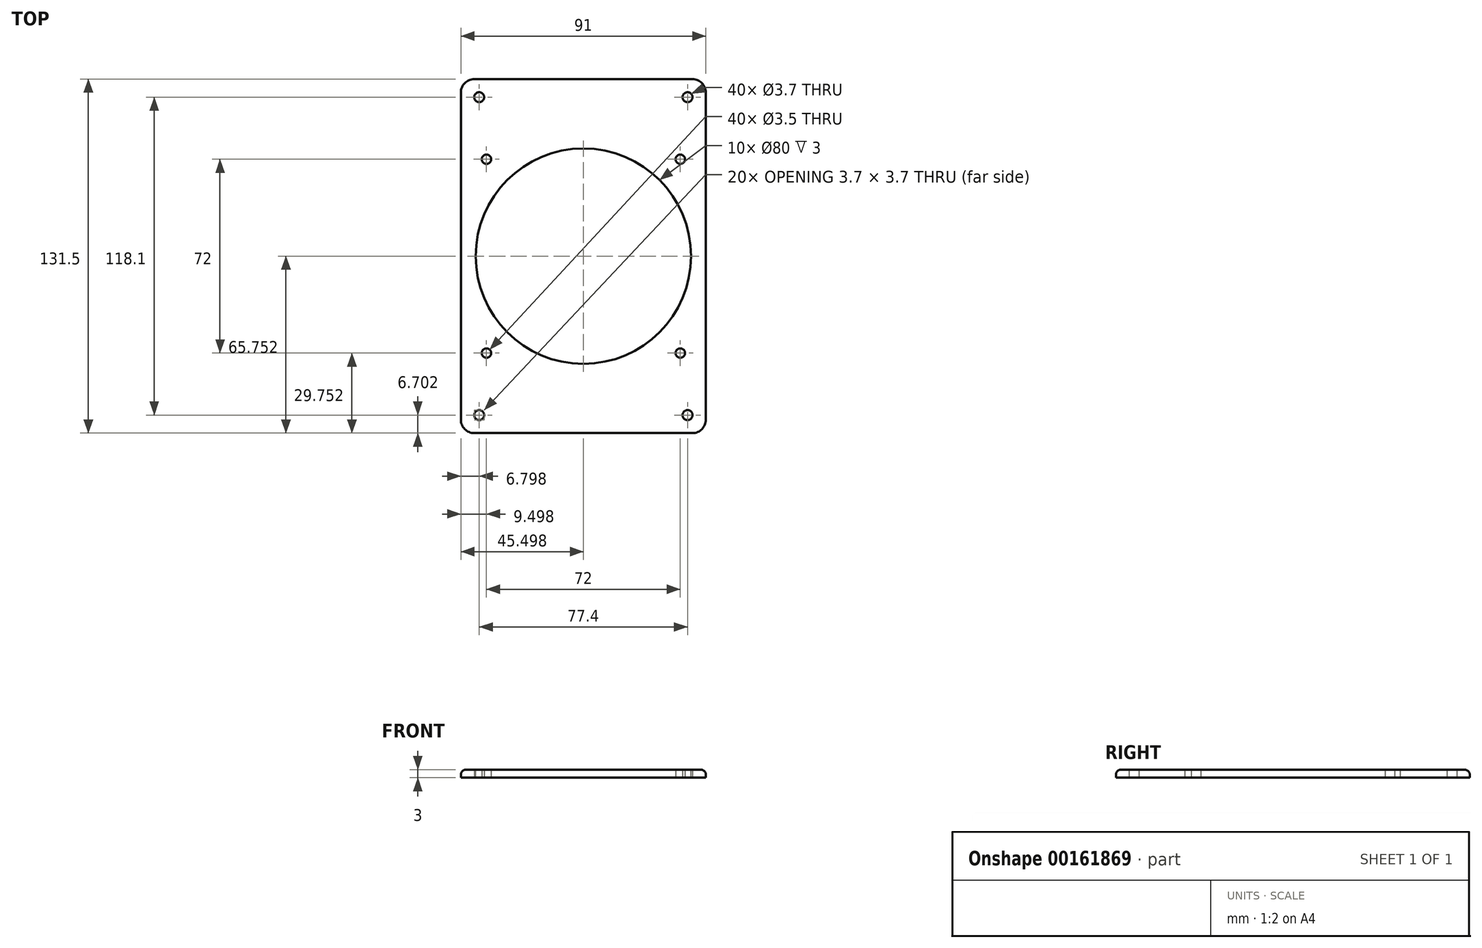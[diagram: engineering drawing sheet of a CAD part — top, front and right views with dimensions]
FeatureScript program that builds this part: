
annotation { "Feature Type Name" : "Feature", "Feature Type Description" : "" }
export const myFeature = defineFeature(function(context is Context, id is Id, definition is map)
    precondition{}
    {
        {
            var Q0;
            Q0=qCreatedBy(makeId("Top.planeOp"),FACE);
            var sketch = newSketch(context, id + "F0", { "sketchPlane" : qUnion([Q0])});
            skLineSegment(sketch, "E0.bottom", {"start": v(54.26, -33.58) * mm, "end": v(-26.74, -33.58) * mm});
            skLineSegment(sketch, "E0.top", {"start": v(54.26, 97.92) * mm, "end": v(-26.74, 97.92) * mm});
            skLineSegment(sketch, "E0.left", {"start": v(59.26, -28.58) * mm, "end": v(59.26, 92.92) * mm});
            skLineSegment(sketch, "E0.right", {"start": v(-31.74, -28.58) * mm, "end": v(-31.74, 92.92) * mm});
            skLineSegment(sketch, "E1.bottom", {"start": v(80.42, 31.08) * mm, "end": v(80.93, 31.08) * mm});
            skLineSegment(sketch, "E1.top", {"start": v(80.42, 14.88) * mm, "end": v(80.93, 14.88) * mm});
            skPoint(sketch, "E2.visualSharp", {"position": v(-31.74, 97.92) * mm});
            skArc(sketch, "E2.filletArc", {"start": v(-26.74, 97.92) * mm, "mid": v(-30.28, 96.46) * mm, "end": v(-31.74, 92.92) * mm});
            skPoint(sketch, "E3.visualSharp", {"position": v(-31.74, -33.58) * mm});
            skArc(sketch, "E3.filletArc", {"start": v(-31.74, -28.58) * mm, "mid": v(-30.28, -32.11) * mm, "end": v(-26.74, -33.58) * mm});
            skPoint(sketch, "E4.visualSharp", {"position": v(59.26, 97.92) * mm});
            skArc(sketch, "E4.filletArc", {"start": v(59.26, 92.92) * mm, "mid": v(57.8, 96.46) * mm, "end": v(54.26, 97.92) * mm});
            skPoint(sketch, "E5.visualSharp", {"position": v(59.26, -33.58) * mm});
            skArc(sketch, "E5.filletArc", {"start": v(54.26, -33.58) * mm, "mid": v(57.8, -32.11) * mm, "end": v(59.26, -28.58) * mm});
            skSolve(sketch);
        }
        {
            var Q0;
            Q0=makeQuery(id+"F0.imprint","IMPRINT",FACE,{"disambiguationData":[TD([[makeQuery(id+"F0.imprint","IMPRINT",EDGE,{"derivedFrom":sQuery(id+"F0.wireOp",EDGE,"E0.bottom")}),-1.0]])]});
            extrude(context, id + "F1", {"entities" : qUnion([Q0]), "depth" : 3 * mm});
        }
        {
            var Q0;
            Q0=makeQuery(id+"F1.opExtrude","CAP_FACE",FACE,{"disambiguationData":[OSD([sQuery(id+"F0.wireOp",EDGE,"E0.bottom"),sQuery(id+"F0.wireOp",EDGE,"E0.top"),sQuery(id+"F0.wireOp",EDGE,"E0.left"),sQuery(id+"F0.wireOp",EDGE,"E0.right"),sQuery(id+"F0.wireOp",EDGE,"E2.filletArc"),sQuery(id+"F0.wireOp",EDGE,"E3.filletArc"),sQuery(id+"F0.wireOp",EDGE,"E4.filletArc"),sQuery(id+"F0.wireOp",EDGE,"E5.filletArc")])],"isStart":false});
            var sketch = newSketch(context, id + "F2", { "sketchPlane" : qUnion([Q0])});
            skLineSegment(sketch, "E6.bottom", {"start": v(-24.94, 91.22) * mm, "end": v(52.46, 91.22) * mm});
            skLineSegment(sketch, "E6.top", {"start": v(-24.94, -26.88) * mm, "end": v(52.46, -26.88) * mm});
            skLineSegment(sketch, "E6.left", {"start": v(-24.94, 91.22) * mm, "end": v(-24.94, -26.88) * mm});
            skLineSegment(sketch, "E6.right", {"start": v(52.46, 91.22) * mm, "end": v(52.46, -26.88) * mm});
            skPoint(sketch, "E7", {"position": v(-24.94, 91.22) * mm});
            skPoint(sketch, "E8", {"position": v(52.46, 91.22) * mm});
            skPoint(sketch, "E9", {"position": v(52.46, -26.88) * mm});
            skPoint(sketch, "E10", {"position": v(-24.94, -26.88) * mm});
            skSolve(sketch);
        }
        {
            var Q0;
            Q0=sQuery(id+"F2.wireOp",VERTEX,"E7");
            var Q1;
            Q1=sQuery(id+"F2.wireOp",VERTEX,"E8");
            var Q2;
            Q2=sQuery(id+"F2.wireOp",VERTEX,"E9");
            var Q3;
            Q3=sQuery(id+"F2.wireOp",VERTEX,"E10");
            var Q4;
            Q4=makeQuery(id+"F1.opExtrude","SWEPT_BODY",BODY,{"disambiguationData":[OSD([sQuery(id+"F0.wireOp",EDGE,"E0.bottom"),sQuery(id+"F0.wireOp",EDGE,"E0.top"),sQuery(id+"F0.wireOp",EDGE,"E0.left"),sQuery(id+"F0.wireOp",EDGE,"E0.right"),sQuery(id+"F0.wireOp",EDGE,"E2.filletArc"),sQuery(id+"F0.wireOp",EDGE,"E3.filletArc"),sQuery(id+"F0.wireOp",EDGE,"E4.filletArc"),sQuery(id+"F0.wireOp",EDGE,"E5.filletArc")])]});
            hole(context, id + "F3", {"style" : HoleStyle.SIMPLE, "endStyle" : HoleEndStyle.THROUGH, "holeDiameter" : 3.7 * mm, "locations" : qUnion([Q0, Q1, Q2, Q3]), "scope" : qUnion([Q4]), "isTappedThrough" : true});
        }
        {
            var Q0;
            Q0=makeQuery(id+"F1.opExtrude","CAP_FACE",FACE,{"disambiguationData":[OSD([sQuery(id+"F0.wireOp",EDGE,"E0.bottom"),sQuery(id+"F0.wireOp",EDGE,"E0.top"),sQuery(id+"F0.wireOp",EDGE,"E0.left"),sQuery(id+"F0.wireOp",EDGE,"E0.right"),sQuery(id+"F0.wireOp",EDGE,"E2.filletArc"),sQuery(id+"F0.wireOp",EDGE,"E3.filletArc"),sQuery(id+"F0.wireOp",EDGE,"E4.filletArc"),sQuery(id+"F0.wireOp",EDGE,"E5.filletArc")])],"isStart":false});
            var sketch = newSketch(context, id + "F4", { "sketchPlane" : qUnion([Q0])});
            skCircle(sketch, "E11", {"center": v(13.76, 32.17) * mm, "radius": 40 * mm});
            skLineSegment(sketch, "E12.bottom", {"start": v(-22.24, 68.17) * mm, "end": v(49.76, 68.17) * mm});
            skLineSegment(sketch, "E12.top", {"start": v(-22.24, -3.83) * mm, "end": v(49.76, -3.83) * mm});
            skLineSegment(sketch, "E12.left", {"start": v(-22.24, 68.17) * mm, "end": v(-22.24, -3.83) * mm});
            skLineSegment(sketch, "E12.right", {"start": v(49.76, 68.17) * mm, "end": v(49.76, -3.83) * mm});
            skPoint(sketch, "E13", {"position": v(-22.24, 68.17) * mm});
            skPoint(sketch, "E14", {"position": v(49.76, 68.17) * mm});
            skPoint(sketch, "E15", {"position": v(49.76, -3.83) * mm});
            skPoint(sketch, "E16", {"position": v(-22.24, -3.83) * mm});
            skSolve(sketch);
        }
        {
            var Q0;
            Q0=makeQuery(id+"F1.opExtrude","CAP_FACE",FACE,{"disambiguationData":[OSD([sQuery(id+"F0.wireOp",EDGE,"E0.bottom"),sQuery(id+"F0.wireOp",EDGE,"E0.top"),sQuery(id+"F0.wireOp",EDGE,"E0.left"),sQuery(id+"F0.wireOp",EDGE,"E0.right"),sQuery(id+"F0.wireOp",EDGE,"E2.filletArc"),sQuery(id+"F0.wireOp",EDGE,"E3.filletArc"),sQuery(id+"F0.wireOp",EDGE,"E4.filletArc"),sQuery(id+"F0.wireOp",EDGE,"E5.filletArc")])],"isStart":false});
            var sketch = newSketch(context, id + "F5", { "sketchPlane" : qUnion([Q0])});
            skCircle(sketch, "E17", {"center": v(13.76, 32.17) * mm, "radius": 40 * mm});
            skPoint(sketch, "E18", {"position": v(-21.85, 68.29) * mm});
            skPoint(sketch, "E19", {"position": v(49.62, 68.29) * mm});
            skPoint(sketch, "E20", {"position": v(50.13, -3.7) * mm});
            skPoint(sketch, "E21", {"position": v(-22.02, -4.03) * mm});
            skSolve(sketch);
        }
        {
            var Q0;
            Q0=makeQuery(id+"F5.imprint","IMPRINT",FACE,{"disambiguationData":[TD([[makeQuery(id+"F5.imprint","IMPRINT",EDGE,{"derivedFrom":sQuery(id+"F5.wireOp",EDGE,"E17")}),1.0]])]});
            extrude(context, id + "F6", {"entities" : qUnion([Q0]), "operationType" : NewBodyOperationType.REMOVE, "oppositeDirection" : true, "depth" : 25 * mm});
        }
        {
            var Q0;
            Q0=makeQuery(id+"F1.opExtrude","CAP_EDGE",EDGE,{"disambiguationData":[OSD([sQuery(id+"F0.wireOp",EDGE,"E0.right")])],"isStart":false});
            var Q1;
            Q1=makeQuery(id+"F1.opExtrude","CAP_EDGE",EDGE,{"disambiguationData":[OSD([sQuery(id+"F0.wireOp",EDGE,"E0.top")])],"isStart":false});
            fillet(context, id + "F7", {"entities" : qUnion([Q0, Q1]), "radius" : 2 * mm, "tangentPropagation" : true, "allowEdgeOverflow" : false});
        }
        {
            var Q0;
            Q0=sQuery(id+"F4.wireOp",VERTEX,"E13");
            var Q1;
            Q1=sQuery(id+"F4.wireOp",VERTEX,"E14");
            var Q2;
            Q2=sQuery(id+"F4.wireOp",VERTEX,"E15");
            var Q3;
            Q3=sQuery(id+"F4.wireOp",VERTEX,"E16");
            var Q4;
            Q4=makeQuery(id+"F1.opExtrude","SWEPT_BODY",BODY,{"disambiguationData":[OSD([sQuery(id+"F0.wireOp",EDGE,"E0.bottom"),sQuery(id+"F0.wireOp",EDGE,"E0.top"),sQuery(id+"F0.wireOp",EDGE,"E0.left"),sQuery(id+"F0.wireOp",EDGE,"E0.right"),sQuery(id+"F0.wireOp",EDGE,"E2.filletArc"),sQuery(id+"F0.wireOp",EDGE,"E3.filletArc"),sQuery(id+"F0.wireOp",EDGE,"E4.filletArc"),sQuery(id+"F0.wireOp",EDGE,"E5.filletArc")])]});
            hole(context, id + "F8", {"style" : HoleStyle.SIMPLE, "endStyle" : HoleEndStyle.THROUGH, "holeDiameter" : 3.5 * mm, "locations" : qUnion([Q0, Q1, Q2, Q3]), "scope" : qUnion([Q4]), "isTappedThrough" : true});
        }
    });
